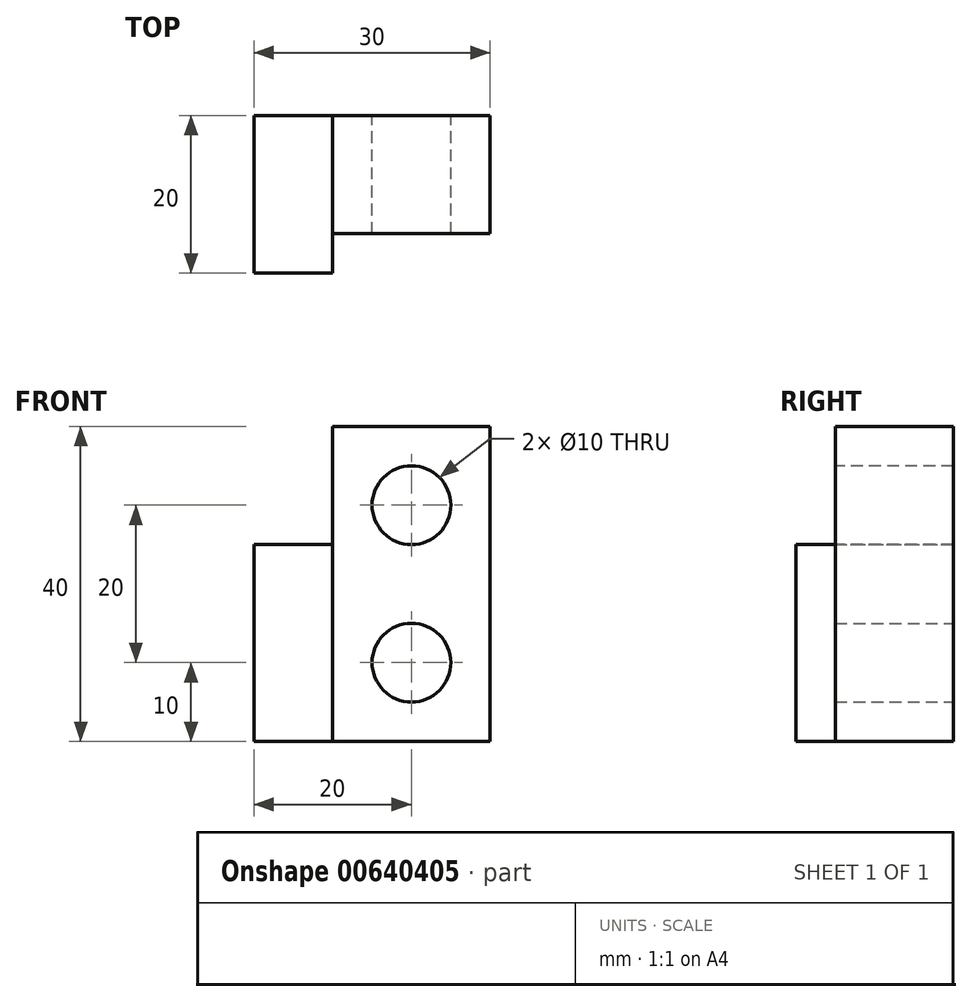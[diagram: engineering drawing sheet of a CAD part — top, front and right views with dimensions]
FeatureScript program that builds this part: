
annotation { "Feature Type Name" : "Feature", "Feature Type Description" : "" }
export const myFeature = defineFeature(function(context is Context, id is Id, definition is map)
    precondition{}
    {
        {
            var Q0;
            Q0=qCreatedBy(makeId("Front.planeOp"),FACE);
            var sketch = newSketch(context, id + "F0", { "sketchPlane" : qUnion([Q0])});
            skLineSegment(sketch, "E0.bottom", {"start": v(-10, 20) * mm, "end": v(10, 20) * mm});
            skLineSegment(sketch, "E0.top", {"start": v(-10, -20) * mm, "end": v(10, -20) * mm});
            skLineSegment(sketch, "E0.left", {"start": v(-10, 20) * mm, "end": v(-10, -20) * mm});
            skLineSegment(sketch, "E0.right", {"start": v(10, 20) * mm, "end": v(10, -20) * mm});
            skPoint(sketch, "E0.middle", {"position": v(0, 0) * mm});
            skLineSegment(sketch, "E1.bottom", {"start": v(-10, -20) * mm, "end": v(-20, -20) * mm});
            skLineSegment(sketch, "E1.top", {"start": v(-10, 5) * mm, "end": v(-20, 5) * mm});
            skLineSegment(sketch, "E1.left", {"start": v(-10, -20) * mm, "end": v(-10, 5) * mm});
            skLineSegment(sketch, "E1.right", {"start": v(-20, -20) * mm, "end": v(-20, 5) * mm});
            skCircle(sketch, "E2", {"center": v(0, -10) * mm, "radius": 5 * mm});
            skSolve(sketch);
        }
        {
            var Q0;
            Q0=makeQuery(id+"F0.imprint","IMPRINT",FACE,{"disambiguationData":[TD([[makeQuery(id+"F0.imprint","IMPRINT",EDGE,{"derivedFrom":sQuery(id+"F0.wireOp",EDGE,"E0.bottom")}),-1.0]])]});
            extrude(context, id + "F1", {"entities" : qUnion([Q0]), "depth" : 15 * mm, "offsetDistance" : 25 * mm});
        }
        {
            var Q0;
            Q0=makeQuery(id+"F0.imprint","IMPRINT",FACE,{"disambiguationData":[TD([[makeQuery(id+"F0.imprint","IMPRINT",EDGE,{"derivedFrom":sQuery(id+"F0.wireOp",EDGE,"E1.bottom")}),-1.0]])]});
            extrude(context, id + "F2", {"entities" : qUnion([Q0]), "operationType" : NewBodyOperationType.ADD, "depth" : 20 * mm, "offsetDistance" : 25 * mm});
        }
        {
            var Q0;
            Q0=makeQuery(id+"F1.opExtrude","CAP_FACE",FACE,{"disambiguationData":[OSD([sQuery(id+"F0.wireOp",EDGE,"E0.bottom"),sQuery(id+"F0.wireOp",EDGE,"E0.top"),sQuery(id+"F0.wireOp",EDGE,"E0.left"),sQuery(id+"F0.wireOp",EDGE,"E0.right"),sQuery(id+"F0.wireOp",EDGE,"E1.left"),sQuery(id+"F0.wireOp",EDGE,"E2")])],"isStart":false});
            var sketch = newSketch(context, id + "F3", { "sketchPlane" : qUnion([Q0])});
            skCircle(sketch, "E3", {"center": v(0, 10) * mm, "radius": 5 * mm});
            skSolve(sketch);
        }
        {
            var Q0;
            Q0=makeQuery(id+"F3.imprint","IMPRINT",FACE,{"disambiguationData":[TD([[makeQuery(id+"F3.imprint","IMPRINT",EDGE,{"derivedFrom":sQuery(id+"F3.wireOp",EDGE,"E3")}),1.0]])]});
            extrude(context, id + "F4", {"entities" : qUnion([Q0]), "operationType" : NewBodyOperationType.REMOVE, "oppositeDirection" : true, "depth" : 25 * mm, "offsetDistance" : 25 * mm});
        }
    });
